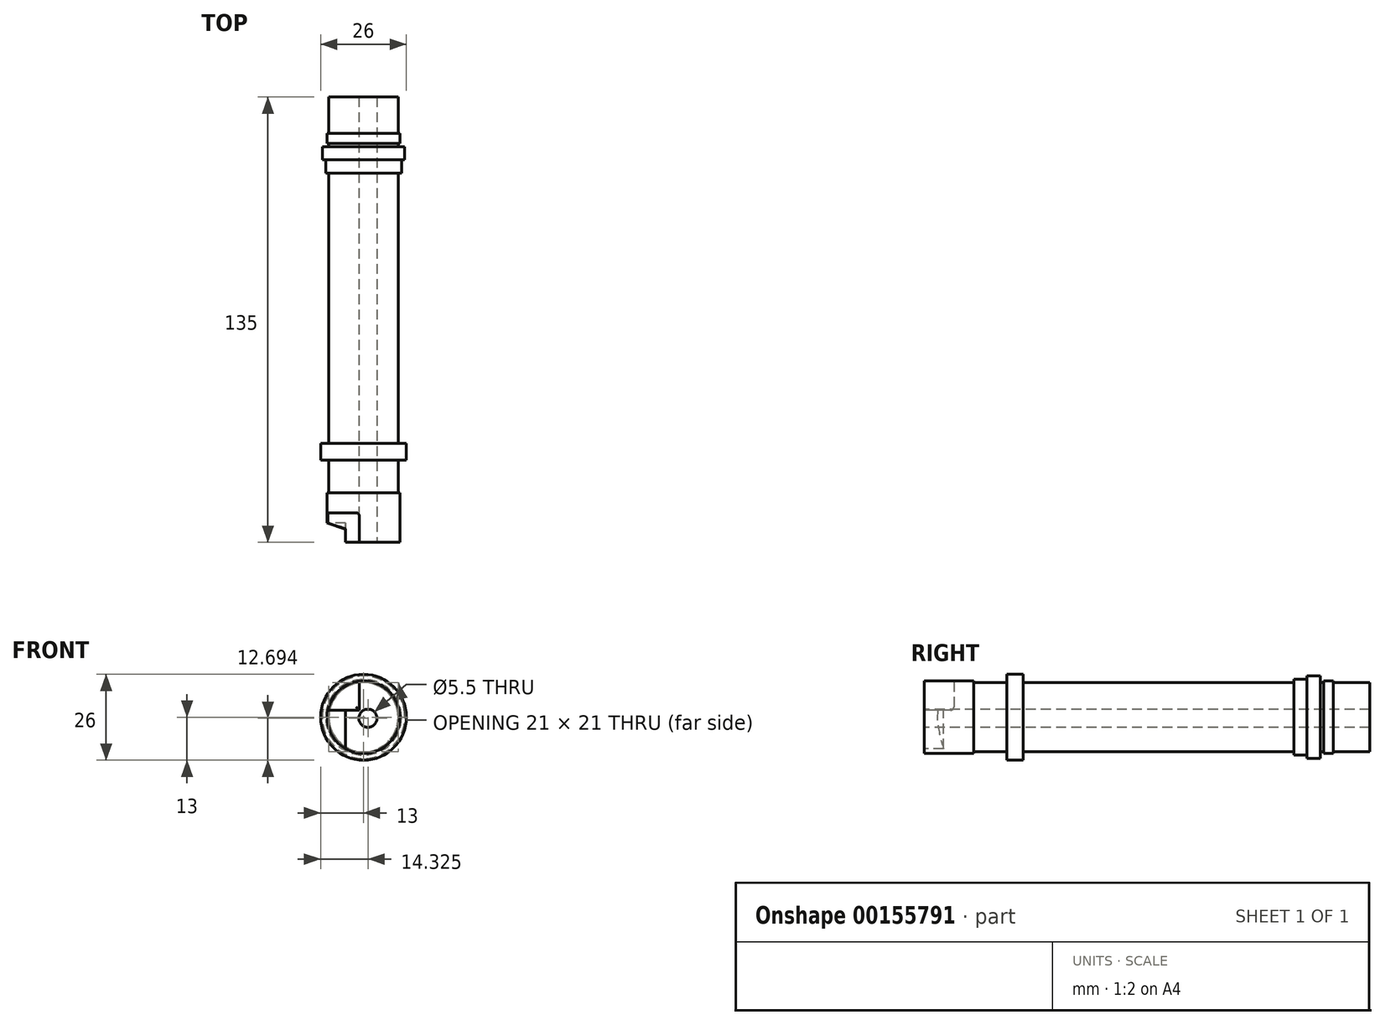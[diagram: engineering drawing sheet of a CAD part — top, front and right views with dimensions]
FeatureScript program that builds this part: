
annotation { "Feature Type Name" : "Feature", "Feature Type Description" : "" }
export const myFeature = defineFeature(function(context is Context, id is Id, definition is map)
    precondition{}
    {
        {
            var Q0;
            Q0=qCreatedBy(makeId("Front.planeOp"),FACE);
            var sketch = newSketch(context, id + "F0", { "sketchPlane" : qUnion([Q0])});
            skLineSegment(sketch, "E0", {"start": v(0, 59.3) * mm, "end": v(0, -56.41) * mm, "construction": true});
            skLineSegment(sketch, "E1", {"start": v(58.11, 0) * mm, "end": v(-58.38, 0) * mm, "construction": true});
            skCircle(sketch, "E2", {"center": v(0, 0) * mm, "radius": 13 * mm});
            skSolve(sketch);
        }
        {
            var Q0;
            Q0 = qSketchRegion(id + "F0", true);
            extrude(context, id + "F1", {"entities" : qUnion([Q0]), "depth" : 5 * mm});
        }
        {
            var Q0;
            Q0=makeQuery(id+"F1.opExtrude","CAP_FACE",FACE,{"disambiguationData":[OSD([sQuery(id+"F0.wireOp",EDGE,"E2")])],"isStart":false});
            var sketch = newSketch(context, id + "F2", { "sketchPlane" : qUnion([Q0])});
            skCircle(sketch, "E3", {"center": v(0, 0) * mm, "radius": 10.5 * mm});
            skSolve(sketch);
        }
        {
            var Q0;
            Q0 = qSketchRegion(id + "F2", true);
            extrude(context, id + "F3", {"entities" : qUnion([Q0]), "operationType" : NewBodyOperationType.ADD, "depth" : 25 * mm, "hasSecondDirection" : true, "secondDirectionOppositeDirection" : true, "secondDirectionDepth" : 110 * mm});
        }
        {
            var Q0;
            Q0=makeQuery(id+"F3.opExtrude","CAP_FACE",FACE,{"disambiguationData":[OSD([sQuery(id+"F2.wireOp",EDGE,"E3")])],"isStart":false});
            var sketch = newSketch(context, id + "F4", { "sketchPlane" : qUnion([Q0])});
            skCircle(sketch, "E4", {"center": v(0, 0) * mm, "radius": 4.5 * mm});
            skSolve(sketch);
        }
        {
            var Q0;
            Q0=makeQuery(id+"F3.opExtrude","CAP_FACE",FACE,{"disambiguationData":[OSD([sQuery(id+"F2.wireOp",EDGE,"E3")])],"isStart":true});
            var sketch = newSketch(context, id + "F5", { "sketchPlane" : qUnion([Q0])});
            skCircle(sketch, "E5", {"center": v(0, 0) * mm, "radius": 11.5 * mm});
            skCircle(sketch, "E6", {"center": v(0, 0) * mm, "radius": 10.5 * mm});
            skSolve(sketch);
        }
        {
            var Q0;
            Q0 = qSketchRegion(id + "F5", true);
            extrude(context, id + "F6", {"entities" : qUnion([Q0]), "operationType" : NewBodyOperationType.ADD, "oppositeDirection" : true, "depth" : 23 * mm, "hasSecondDirection" : true, "secondDirectionOppositeDirection" : true, "secondDirectionDepth" : 19 * mm});
        }
        {
            var Q0;
            Q0=makeQuery(id+"F4.imprint","IMPRINT",FACE,{"disambiguationData":[TD([[makeQuery(id+"F4.imprint","IMPRINT",EDGE,{"derivedFrom":sQuery(id+"F4.wireOp",EDGE,"E4")}),-1.0]])]});
            var sketch = newSketch(context, id + "F7", { "sketchPlane" : qUnion([Q0])});
            skCircle(sketch, "E7", {"center": v(0, 0) * mm, "radius": 11 * mm});
            skCircle(sketch, "E8", {"center": v(0, 0) * mm, "radius": 10.5 * mm});
            skSolve(sketch);
        }
        {
            var Q0;
            Q0 = qSketchRegion(id + "F7", true);
            extrude(context, id + "F8", {"entities" : qUnion([Q0]), "operationType" : NewBodyOperationType.ADD, "oppositeDirection" : true, "depth" : 15 * mm});
        }
        {
            var Q0;
            Q0=makeQuery(id+"F4.imprint","IMPRINT",FACE,{"disambiguationData":[TD([[makeQuery(id+"F4.imprint","IMPRINT",EDGE,{"derivedFrom":sQuery(id+"F4.wireOp",EDGE,"E4")}),-1.0]])]});
            var sketch = newSketch(context, id + "F9", { "sketchPlane" : qUnion([Q0])});
            skLineSegment(sketch, "E9", {"start": v(-1.3, 10.92) * mm, "end": v(-1.3, 2.12) * mm});
            skLineSegment(sketch, "E10", {"start": v(-1.3, 2.12) * mm, "end": v(-10.84, 2.12) * mm});
            skArc(sketch, "E11", {"start": v(-1.3, 10.92) * mm, "mid": v(-7.5, 8.08) * mm, "end": v(-10.84, 2.12) * mm});
            skSolve(sketch);
        }
        {
            var Q0;
            Q0 = qSketchRegion(id + "F9", true);
            extrude(context, id + "F10", {"entities" : qUnion([Q0]), "operationType" : NewBodyOperationType.REMOVE, "oppositeDirection" : true, "depth" : 9 * mm});
        }
        {
            var Q0;
            Q0=makeQuery(id+"F10.boolean.opBoolean","COPY",EDGE,{"derivedFrom":makeQuery(id+"F10.opExtrude","CAP_EDGE",EDGE,{"disambiguationData":[OSD([sQuery(id+"F9.wireOp",EDGE,"E10")])],"isStart":false})});
            var Q1;
            Q1=makeQuery(id+"F10.boolean.opBoolean","COPY",EDGE,{"derivedFrom":makeQuery(id+"F10.opExtrude","CAP_EDGE",EDGE,{"disambiguationData":[OSD([sQuery(id+"F9.wireOp",EDGE,"E9")])],"isStart":false})});
            fillet(context, id + "F11", {"entities" : qUnion([Q0, Q1]), "radius" : 1 * mm, "tangentPropagation" : true, "allowEdgeOverflow" : false});
        }
        {
            var Q0;
            Q0=makeQuery(id+"F10.boolean.opBoolean","COPY",FACE,{"derivedFrom":makeQuery(id+"F10.opExtrude","SWEPT_FACE",FACE,{"disambiguationData":[OSD([sQuery(id+"F9.wireOp",EDGE,"E10")])]})});
            var sketch = newSketch(context, id + "F12", { "sketchPlane" : qUnion([Q0])});
            skLineSegment(sketch, "E12", {"start": v(-5.5, -26.15) * mm, "end": v(-5.5, -30) * mm});
            skLineSegment(sketch, "E13", {"start": v(-5.5, -26.15) * mm, "end": v(-14.07, -26.15) * mm});
            skLineSegment(sketch, "E14", {"start": v(-14.07, -26.15) * mm, "end": v(-14.07, -30) * mm});
            skLineSegment(sketch, "E15", {"start": v(-14.07, -30) * mm, "end": v(-5.5, -30) * mm});
            skSolve(sketch);
        }
        {
            var Q0;
            Q0 = qSketchRegion(id + "F12", true);
            extrude(context, id + "F13", {"entities" : qUnion([Q0]), "operationType" : NewBodyOperationType.REMOVE, "oppositeDirection" : true, "depth" : 30 * mm});
        }
        {
            var Q0;
            Q0=makeQuery(id+"F13.boolean.opBoolean","INTERSECT",EDGE,{"derivedFrom":[makeQuery(id+"F8.opExtrude","SWEPT_FACE",FACE,{"disambiguationData":[OSD([sQuery(id+"F7.wireOp",EDGE,"E7")])]}),makeQuery(id+"F13.opExtrude","SWEPT_FACE",FACE,{"disambiguationData":[OSD([sQuery(id+"F12.wireOp",EDGE,"E13")])]})]});
            chamfer(context, id + "F14", {"entities" : qUnion([Q0]), "chamferType" : ChamferType.TWO_OFFSETS, "width1" : 6 * mm, "oppositeDirection" : false, "width2" : 2 * mm, "tangentPropagation" : true});
        }
        {
            var Q0;
            Q0=makeQuery(id+"F3.opExtrude","CAP_FACE",FACE,{"disambiguationData":[OSD([sQuery(id+"F2.wireOp",EDGE,"E3")])],"isStart":true});
            var sketch = newSketch(context, id + "F15", { "sketchPlane" : qUnion([Q0])});
            skCircle(sketch, "E16", {"center": v(0, 0) * mm, "radius": 12.5 * mm});
            skCircle(sketch, "E17", {"center": v(0, 0) * mm, "radius": 10.5 * mm});
            skSolve(sketch);
        }
        {
            var Q0;
            Q0 = qSketchRegion(id + "F15", true);
            extrude(context, id + "F16", {"entities" : qUnion([Q0]), "operationType" : NewBodyOperationType.ADD, "oppositeDirection" : true, "depth" : 19 * mm, "hasSecondDirection" : true, "secondDirectionOppositeDirection" : true, "secondDirectionDepth" : 15 * mm});
        }
        {
            var Q0;
            Q0=makeQuery(id+"F3.opExtrude","CAP_FACE",FACE,{"disambiguationData":[OSD([sQuery(id+"F2.wireOp",EDGE,"E3")])],"isStart":true});
            var sketch = newSketch(context, id + "F17", { "sketchPlane" : qUnion([Q0])});
            skCircle(sketch, "E18", {"center": v(0, 0) * mm, "radius": 10.5 * mm});
            skCircle(sketch, "E19", {"center": v(0, 0) * mm, "radius": 11 * mm});
            skSolve(sketch);
        }
        {
            var Q0;
            Q0 = qSketchRegion(id + "F17", true);
            extrude(context, id + "F18", {"entities" : qUnion([Q0]), "operationType" : NewBodyOperationType.ADD, "oppositeDirection" : true, "depth" : 14 * mm, "hasSecondDirection" : true, "secondDirectionOppositeDirection" : true, "secondDirectionDepth" : 11 * mm});
        }
        {
            var Q0;
            Q0=makeQuery(id+"F4.imprint","IMPRINT",FACE,{"disambiguationData":[TD([[makeQuery(id+"F4.imprint","IMPRINT",EDGE,{"derivedFrom":sQuery(id+"F4.wireOp",EDGE,"E4")}),-1.0]])]});
            var sketch = newSketch(context, id + "F19", { "sketchPlane" : qUnion([Q0])});
            skCircle(sketch, "E20", {"center": v(1.33, -0.3) * mm, "radius": 2.75 * mm});
            skSolve(sketch);
        }
        {
            var Q0;
            Q0 = qSketchRegion(id + "F19", true);
            extrude(context, id + "F20", {"entities" : qUnion([Q0]), "operationType" : NewBodyOperationType.REMOVE, "oppositeDirection" : true, "depth" : 148 * mm});
        }
    });
